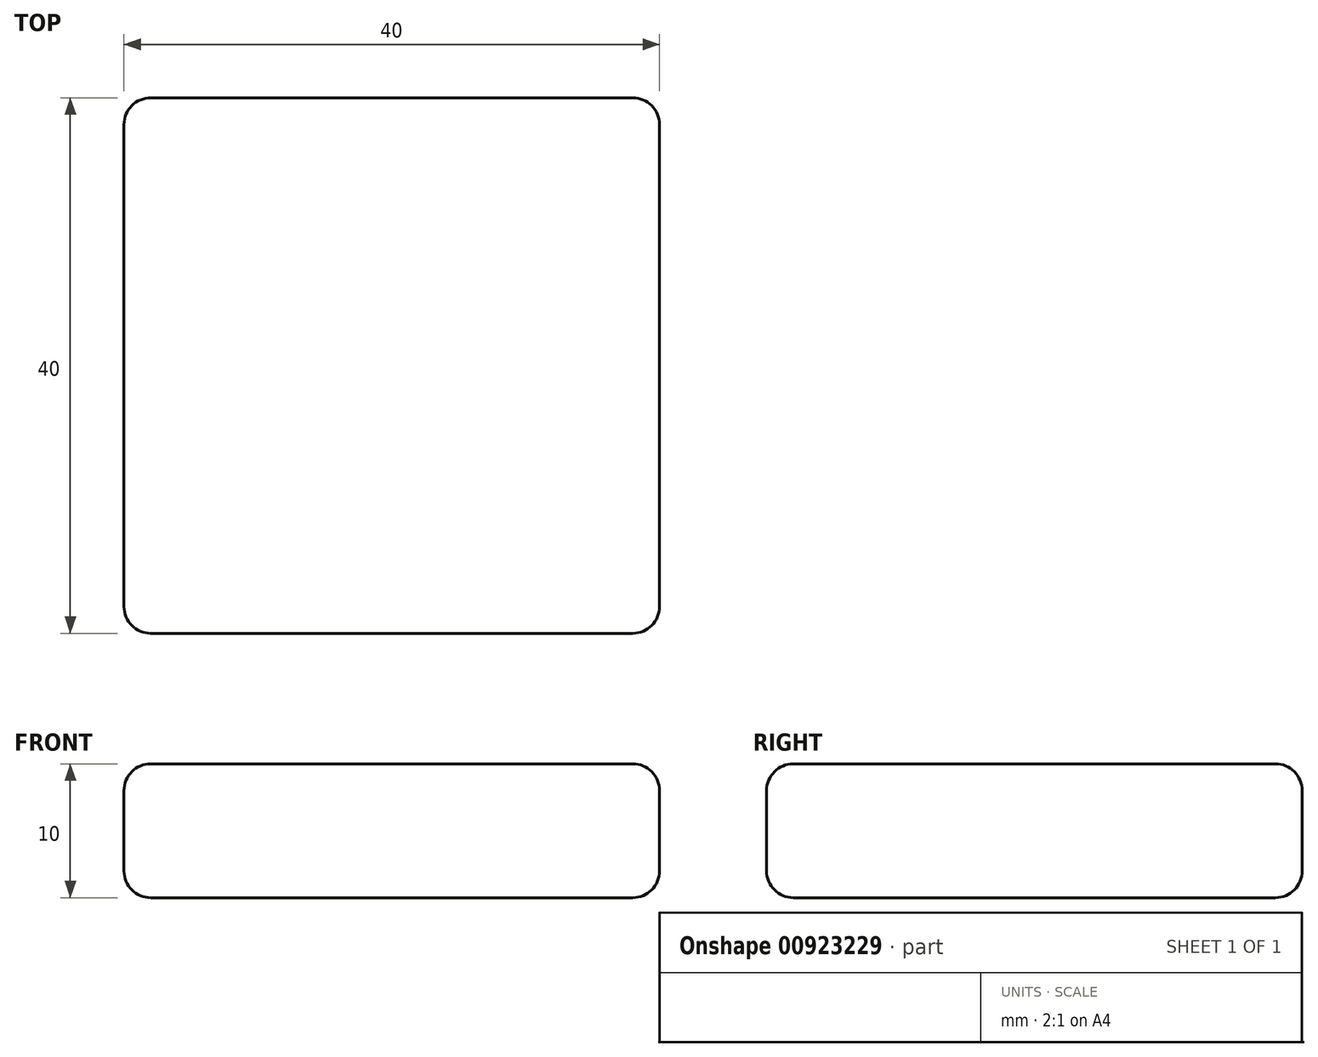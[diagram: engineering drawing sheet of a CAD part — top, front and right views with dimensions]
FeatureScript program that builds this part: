
annotation { "Feature Type Name" : "Feature", "Feature Type Description" : "" }
export const myFeature = defineFeature(function(context is Context, id is Id, definition is map)
    precondition{}
    {
        {
            var Q0;
            Q0=qCreatedBy(makeId("Top.planeOp"),FACE);
            var sketch = newSketch(context, id + "F0", { "sketchPlane" : qUnion([Q0])});
            skLineSegment(sketch, "E0.bottom", {"start": v(20, 20) * mm, "end": v(-20, 20) * mm});
            skLineSegment(sketch, "E0.top", {"start": v(20, -20) * mm, "end": v(-20, -20) * mm});
            skLineSegment(sketch, "E0.left", {"start": v(20, 20) * mm, "end": v(20, -20) * mm});
            skLineSegment(sketch, "E0.right", {"start": v(-20, 20) * mm, "end": v(-20, -20) * mm});
            skPoint(sketch, "E0.middle", {"position": v(0, 0) * mm});
            skSolve(sketch);
        }
        {
            var Q0;
            Q0=makeQuery(id+"F0.imprint","IMPRINT",FACE,{"disambiguationData":[TD([[makeQuery(id+"F0.imprint","IMPRINT",EDGE,{"derivedFrom":sQuery(id+"F0.wireOp",EDGE,"E0.bottom")}),1.0]])]});
            extrude(context, id + "F1", {"entities" : qUnion([Q0]), "depth" : 10 * mm, "offsetDistance" : 25.4 * mm});
        }
        {
            var Q0;
            Q0=makeQuery(id+"F1.opExtrude","CAP_EDGE",EDGE,{"disambiguationData":[OSD([sQuery(id+"F0.wireOp",EDGE,"E0.left")])],"isStart":false});
            var Q1;
            Q1=makeQuery(id+"F1.opExtrude","CAP_EDGE",EDGE,{"disambiguationData":[OSD([sQuery(id+"F0.wireOp",EDGE,"E0.top")])],"isStart":false});
            var Q2;
            Q2=makeQuery(id+"F1.opExtrude","CAP_EDGE",EDGE,{"disambiguationData":[OSD([sQuery(id+"F0.wireOp",EDGE,"E0.right")])],"isStart":false});
            var Q3;
            Q3=makeQuery(id+"F1.opExtrude","CAP_EDGE",EDGE,{"disambiguationData":[OSD([sQuery(id+"F0.wireOp",EDGE,"E0.bottom")])],"isStart":false});
            var Q4;
            Q4=makeQuery(id+"F1.opExtrude","SWEPT_EDGE",EDGE,{"disambiguationData":[OSD([sQuery(id+"F0.wireOp",EDGE,"E0.top"),sQuery(id+"F0.wireOp",EDGE,"E0.left")])]});
            var Q5;
            Q5=makeQuery(id+"F1.opExtrude","SWEPT_EDGE",EDGE,{"disambiguationData":[OSD([sQuery(id+"F0.wireOp",EDGE,"E0.top"),sQuery(id+"F0.wireOp",EDGE,"E0.right")])]});
            var Q6;
            Q6=makeQuery(id+"F1.opExtrude","SWEPT_EDGE",EDGE,{"disambiguationData":[OSD([sQuery(id+"F0.wireOp",EDGE,"E0.bottom"),sQuery(id+"F0.wireOp",EDGE,"E0.left")])]});
            var Q7;
            Q7=makeQuery(id+"F1.opExtrude","SWEPT_EDGE",EDGE,{"disambiguationData":[OSD([sQuery(id+"F0.wireOp",EDGE,"E0.bottom"),sQuery(id+"F0.wireOp",EDGE,"E0.right")])]});
            var Q8;
            Q8=makeQuery(id+"F1.opExtrude","CAP_EDGE",EDGE,{"disambiguationData":[OSD([sQuery(id+"F0.wireOp",EDGE,"E0.bottom")])],"isStart":true});
            var Q9;
            Q9=makeQuery(id+"F1.opExtrude","CAP_EDGE",EDGE,{"disambiguationData":[OSD([sQuery(id+"F0.wireOp",EDGE,"E0.right")])],"isStart":true});
            var Q10;
            Q10=makeQuery(id+"F1.opExtrude","CAP_EDGE",EDGE,{"disambiguationData":[OSD([sQuery(id+"F0.wireOp",EDGE,"E0.left")])],"isStart":true});
            var Q11;
            Q11=makeQuery(id+"F1.opExtrude","CAP_EDGE",EDGE,{"disambiguationData":[OSD([sQuery(id+"F0.wireOp",EDGE,"E0.top")])],"isStart":true});
            fillet(context, id + "F2", {"entities" : qUnion([Q0, Q1, Q2, Q3, Q4, Q5, Q6, Q7, Q8, Q9, Q10, Q11]), "radius" : 2 * mm, "tangentPropagation" : true, "allowEdgeOverflow" : false});
        }
    });
